FCSTD DOCUMENT  (FreeCAD 0.16R)
Label: WedgeRisers
License: All rights reserved
LicenseURL: http://en.wikipedia.org/wiki/All_rights_reserved
objects: Sketcher::SketchObject×3, PartDesign::Pocket×2, PartDesign::Pad×1, Mesh::Feature×1
note: 9 computed .brp shape members not serialized (recipe doc carries the construction recipe); baked Part::Feature solids carry a one-line shape summary decoded from their .brp

FEATURE [Sketcher::SketchObject] Sketch
  Placement = pos=(0,0,0) rot=(-1,0,0;4.71239rad)
  sketch-geometry (3):
    g0: LineSegment StartX=-45 StartY=0 StartZ=0 EndX=-44.0562 EndY=13 EndZ=0
    g1: LineSegment StartX=-44.0562 StartY=13 StartZ=0 EndX=45 EndY=0 EndZ=0
    g2: LineSegment StartX=45 StartY=0 StartZ=0 EndX=-45 EndY=0 EndZ=0
  constraints (9):
    c: Coincident(g0,g1)
    c: Coincident(g1,g2)
    c: Coincident(g2,g0)
    c: Horizontal(g2)
    c: DistanceY(g0,g0) = 13
    c: DistanceX(g2,g2) = 90
    c: DistanceY(g-1,g0) = 0
    c: Symmetric(g0,g1,g-2)
    c: Distance(g1) = 90
FEATURE [PartDesign::Pad] Pad
  Length = 52
  Length2 = 100
  Placement = pos=(0,0,0) rot=(-1,0,0;4.71239rad)
  Sketch = -> Sketch
  Type = 0
FEATURE [Sketcher::SketchObject] Sketch001
  Placement = pos=(0,-52,0) rot=(1,0,0;1.5708rad)
  Support = -> Pad [Face5]
  sketch-geometry (4):
    g0: LineSegment StartX=29.7041 StartY=7.46774 StartZ=0 EndX=41.289 EndY=7.46774 EndZ=0
    g1: LineSegment StartX=41.289 StartY=7.46774 StartZ=0 EndX=41.289 EndY=-4.11716 EndZ=0
    g2: LineSegment StartX=41.289 StartY=-4.11716 StartZ=0 EndX=29.7041 EndY=-4.11716 EndZ=0
    g3: LineSegment StartX=29.7041 StartY=-4.11716 StartZ=0 EndX=29.7041 EndY=7.46774 EndZ=0
  constraints (14):
    c: Coincident(g0,g1)
    c: Coincident(g1,g2)
    c: Coincident(g2,g3)
    c: Coincident(g3,g0)
    c: Horizontal(g0)
    c: Horizontal(g2)
    c: Vertical(g1)
    c: Vertical(g3)
    c: Equal(g0,g1)
    c: Equal(g1,g2)
    c: Equal(g2,g3)
    c: DistanceX(g-1,g0) = 29.7041
    c: DistanceY(g-1,g0) = 7.46774
    c: DistanceX(g0,g0) = 11.5849
FEATURE [PartDesign::Pocket] Pocket
  Length = 5
  Placement = pos=(0,0,0) rot=(-1,0,0;4.71239rad)
  Sketch = -> Sketch001
  Type = 1
FEATURE [Sketcher::SketchObject] Sketch002
  ExternalGeometry = -> [Pocket]
  Placement = pos=(0,0,0) rot=(1,0,0;3.14159rad)
  Support = -> Pocket [Face2]
  sketch-geometry (8):
    g0: LineSegment [constr] StartX=-38 StartY=46.5 StartZ=0 EndX=25 EndY=46.5 EndZ=0
    g1: LineSegment [constr] StartX=25 StartY=46.5 StartZ=0 EndX=25 EndY=5 EndZ=0
    g2: LineSegment [constr] StartX=25 StartY=5 StartZ=0 EndX=-38 EndY=5 EndZ=0
    g3: LineSegment [constr] StartX=-38 StartY=5 StartZ=0 EndX=-38 EndY=46.5 EndZ=0
    g4: Circle CenterX=-38 CenterY=46.5 CenterZ=0 NormalX=0 NormalY=0 NormalZ=1 Radius=3
    g5: Circle CenterX=25 CenterY=46.5 CenterZ=0 NormalX=0 NormalY=0 NormalZ=1 Radius=3
    g6: Circle CenterX=-38 CenterY=5 CenterZ=0 NormalX=0 NormalY=0 NormalZ=1 Radius=3
    g7: Circle CenterX=25 CenterY=5 CenterZ=0 NormalX=0 NormalY=0 NormalZ=1 Radius=3
  constraints (20):
    c: Coincident(g0,g1)
    c: Coincident(g1,g2)
    c: Coincident(g2,g3)
    c: Coincident(g3,g0)
    c: Horizontal(g0)
    c: Horizontal(g2)
    c: Vertical(g1)
    c: Vertical(g3)
    c: DistanceX(g0,g0) = 63
    c: DistanceY(g1,g1) = 41.5
    c: DistanceY(g-1,g2) = 5
    c: DistanceX(g2,g-1) = 38
    c: Coincident(g4,g0)
    c: Coincident(g5,g0)
    c: Coincident(g6,g2)
    c: Coincident(g7,g1)
    c: Radius(g4) = 3
    c: Equal(g4,g5)
    c: Equal(g4,g7)
    c: Equal(g4,g6)
FEATURE [PartDesign::Pocket] Pocket001
  Length = 5
  Placement = pos=(0,0,0) rot=(-1,0,0;4.71239rad)
  Sketch = -> Sketch002
  Type = 1
FEATURE [Mesh::Feature] Mesh  label="Pocket001 (Meshed)"
